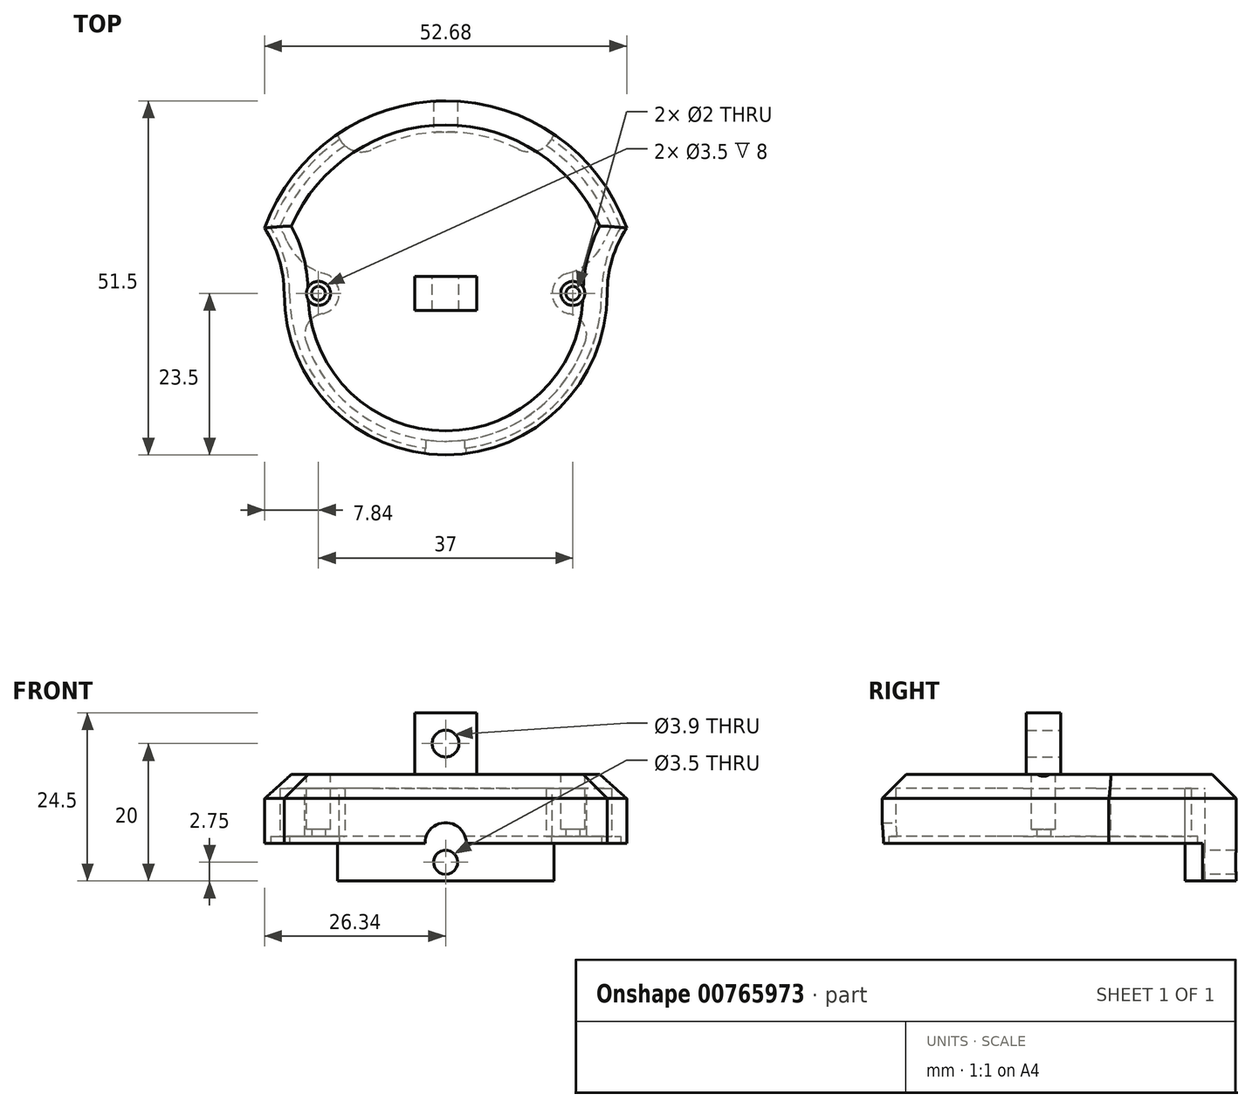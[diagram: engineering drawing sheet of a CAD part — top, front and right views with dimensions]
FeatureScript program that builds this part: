
annotation { "Feature Type Name" : "Feature", "Feature Type Description" : "" }
export const myFeature = defineFeature(function(context is Context, id is Id, definition is map)
    precondition{}
    {
        {
            var Q0;
            Q0=qCreatedBy(makeId("Top.planeOp"),FACE);
            var sketch = newSketch(context, id + "F0", { "sketchPlane" : qUnion([Q0])});
            skCircle(sketch, "E0", {"center": v(0, 0) * mm, "radius": 23.5 * mm, "construction": true});
            skCircle(sketch, "E1", {"center": v(0, 0) * mm, "radius": 28 * mm, "construction": true});
            skLineSegment(sketch, "E2", {"start": v(-26.34, 9.5) * mm, "end": v(26.34, 9.5) * mm, "construction": true});
            skArc(sketch, "E3", {"start": v(-23.5, 0) * mm, "mid": v(0, -23.5) * mm, "end": v(23.5, 0) * mm});
            skArc(sketch, "E4", {"start": v(-26.34, 9.5) * mm, "mid": v(0, 28) * mm, "end": v(26.34, 9.5) * mm});
            skArc(sketch, "E5", {"start": v(-23.5, 0) * mm, "mid": v(-24.22, 4.96) * mm, "end": v(-26.34, 9.5) * mm});
            skArc(sketch, "E6", {"start": v(26.34, 9.5) * mm, "mid": v(24.22, 4.96) * mm, "end": v(23.5, 0) * mm});
            skCircle(sketch, "E7", {"center": v(-18.5, 0) * mm, "radius": 1 * mm});
            skCircle(sketch, "E8", {"center": v(18.5, 0) * mm, "radius": 1 * mm});
            skSolve(sketch);
        }
        {
            var Q0;
            Q0 = qSketchRegion(id + "F0", true);
            extrude(context, id + "F1", {"entities" : qUnion([Q0]), "endBound" : BoundingType.SYMMETRIC, "depth" : 10 * mm, "offsetDistance" : 25 * mm});
        }
        {
            var Q0;
            Q0=makeQuery(id+"F1.opExtrude","CAP_FACE",FACE,{"disambiguationData":[OSD([sQuery(id+"F0.wireOp",EDGE,"E3"),sQuery(id+"F0.wireOp",EDGE,"E4"),sQuery(id+"F0.wireOp",EDGE,"E5"),sQuery(id+"F0.wireOp",EDGE,"E6"),sQuery(id+"F0.wireOp",EDGE,"E7"),sQuery(id+"F0.wireOp",EDGE,"E8")])],"isStart":true});
            var sketch = newSketch(context, id + "F2", { "sketchPlane" : qUnion([Q0])});
            skArc(sketch, "E9", {"start": v(-21.5, 0) * mm, "mid": v(0, 21.5) * mm, "end": v(21.5, 0) * mm});
            skArc(sketch, "E10", {"start": v(-24.12, -9.7) * mm, "mid": v(0, -26) * mm, "end": v(24.12, -9.7) * mm});
            skArc(sketch, "E11", {"start": v(21.5, 0) * mm, "mid": v(22.17, -5.02) * mm, "end": v(24.12, -9.7) * mm});
            skArc(sketch, "E12", {"start": v(-24.12, -9.7) * mm, "mid": v(-22.17, -5.02) * mm, "end": v(-21.5, 0) * mm});
            skSolve(sketch);
        }
        {
            var Q0;
            Q0 = qSketchRegion(id + "F2", true);
            extrude(context, id + "F3", {"entities" : qUnion([Q0]), "operationType" : NewBodyOperationType.REMOVE, "oppositeDirection" : true, "depth" : 8 * mm, "offsetDistance" : 25 * mm});
        }
        {
            var Q0;
            Q0=makeQuery(id+"F1.opExtrude","CAP_FACE",FACE,{"disambiguationData":[OSD([sQuery(id+"F0.wireOp",EDGE,"E3"),sQuery(id+"F0.wireOp",EDGE,"E4"),sQuery(id+"F0.wireOp",EDGE,"E5"),sQuery(id+"F0.wireOp",EDGE,"E6"),sQuery(id+"F0.wireOp",EDGE,"E7"),sQuery(id+"F0.wireOp",EDGE,"E8")])],"isStart":true});
            var sketch = newSketch(context, id + "F4", { "sketchPlane" : qUnion([Q0])});
            skArc(sketch, "E13", {"start": v(-22.7, 0) * mm, "mid": v(0, 22.7) * mm, "end": v(22.7, 0) * mm});
            skArc(sketch, "E14", {"start": v(-25.46, -9.58) * mm, "mid": v(0, -27.2) * mm, "end": v(25.46, -9.58) * mm});
            skArc(sketch, "E15", {"start": v(-25.46, -9.58) * mm, "mid": v(-23.4, -4.99) * mm, "end": v(-22.7, 0) * mm});
            skArc(sketch, "E16", {"start": v(22.7, 0) * mm, "mid": v(23.4, -4.99) * mm, "end": v(25.46, -9.58) * mm});
            skSolve(sketch);
        }
        {
            var Q0;
            Q0 = qSketchRegion(id + "F4", true);
            extrude(context, id + "F5", {"entities" : qUnion([Q0]), "operationType" : NewBodyOperationType.REMOVE, "oppositeDirection" : true, "depth" : 1 * mm, "offsetDistance" : 25 * mm});
        }
        {
            var Q0;
            Q0=makeQuery(id+"F3.boolean.opBoolean","COPY",FACE,{"derivedFrom":makeQuery(id+"F3.opExtrude","CAP_FACE",FACE,{"disambiguationData":[OSD([sQuery(id+"F2.wireOp",EDGE,"E9"),sQuery(id+"F2.wireOp",EDGE,"E10"),sQuery(id+"F2.wireOp",EDGE,"E11"),sQuery(id+"F2.wireOp",EDGE,"E12")])],"isStart":false})});
            var sketch = newSketch(context, id + "F6", { "sketchPlane" : qUnion([Q0])});
            skCircle(sketch, "E17", {"center": v(-18.5, 0) * mm, "radius": 1 * mm});
            skCircle(sketch, "E18", {"center": v(18.5, 0) * mm, "radius": 1 * mm});
            skArc(sketch, "E19", {"start": v(-17.97, 2.96) * mm, "mid": v(-15.5, 0.15) * mm, "end": v(-17.67, -2.89) * mm});
            skArc(sketch, "E20", {"start": v(17.97, 2.96) * mm, "mid": v(15.5, 0.15) * mm, "end": v(17.67, -2.89) * mm});
            skArc(sketch, "E21", {"start": v(-20.33, 6.99) * mm, "mid": v(-20.08, 4.43) * mm, "end": v(-17.97, 2.96) * mm});
            skArc(sketch, "E22", {"start": v(-17.67, -2.89) * mm, "mid": v(-20.91, -4.66) * mm, "end": v(-23.08, -7.64) * mm});
            skArc(sketch, "E23", {"start": v(23.08, -7.64) * mm, "mid": v(20.91, -4.66) * mm, "end": v(17.67, -2.89) * mm});
            skArc(sketch, "E24", {"start": v(17.97, 2.96) * mm, "mid": v(20.08, 4.43) * mm, "end": v(20.33, 6.99) * mm});
            skArc(sketch, "E25", {"start": v(-20.33, 6.99) * mm, "mid": v(-22.85, -0.11) * mm, "end": v(-23.08, -7.64) * mm});
            skArc(sketch, "E26", {"start": v(23.08, -7.64) * mm, "mid": v(22.92, -0.1) * mm, "end": v(20.33, 6.99) * mm});
            skSolve(sketch);
        }
        {
            var Q0;
            Q0 = qSketchRegion(id + "F6", true);
            var Q1;
            Q1=makeQuery(id+"F5.boolean.opBoolean","COPY",FACE,{"derivedFrom":makeQuery(id+"F5.opExtrude","CAP_FACE",FACE,{"disambiguationData":[OSD([sQuery(id+"F4.wireOp",EDGE,"E13"),sQuery(id+"F4.wireOp",EDGE,"E14"),sQuery(id+"F4.wireOp",EDGE,"E15"),sQuery(id+"F4.wireOp",EDGE,"E16")])],"isStart":false})});
            extrude(context, id + "F7", {"entities" : qUnion([Q0]), "operationType" : NewBodyOperationType.ADD, "endBound" : BoundingType.UP_TO_SURFACE, "depth" : 25 * mm, "endBoundEntityFace" : qUnion([Q1]), "offsetDistance" : 25 * mm});
        }
        {
            var Q0;
            Q0=makeQuery(id+"F1.opExtrude","CAP_FACE",FACE,{"disambiguationData":[OSD([sQuery(id+"F0.wireOp",EDGE,"E3"),sQuery(id+"F0.wireOp",EDGE,"E4"),sQuery(id+"F0.wireOp",EDGE,"E5"),sQuery(id+"F0.wireOp",EDGE,"E6"),sQuery(id+"F0.wireOp",EDGE,"E7"),sQuery(id+"F0.wireOp",EDGE,"E8")])],"isStart":false});
            var sketch = newSketch(context, id + "F8", { "sketchPlane" : qUnion([Q0])});
            skCircle(sketch, "E27", {"center": v(-18.5, 0) * mm, "radius": 1.75 * mm});
            skCircle(sketch, "E28", {"center": v(18.5, 0) * mm, "radius": 1.75 * mm});
            skSolve(sketch);
        }
        {
            var Q0;
            Q0 = qSketchRegion(id + "F8", true);
            extrude(context, id + "F9", {"entities" : qUnion([Q0]), "operationType" : NewBodyOperationType.REMOVE, "oppositeDirection" : true, "depth" : 8 * mm, "offsetDistance" : 25 * mm});
        }
        {
            var Q0;
            Q0=qCreatedBy(makeId("Front.planeOp"),FACE);
            var sketch = newSketch(context, id + "F10", { "sketchPlane" : qUnion([Q0])});
            skCircle(sketch, "E29", {"center": v(0, -5) * mm, "radius": 3 * mm});
            skSolve(sketch);
        }
        {
            var Q0;
            Q0 = qSketchRegion(id + "F10", true);
            extrude(context, id + "F11", {"entities" : qUnion([Q0]), "operationType" : NewBodyOperationType.REMOVE, "endBound" : BoundingType.THROUGH_ALL, "depth" : 25 * mm, "offsetDistance" : 25 * mm});
        }
        {
            var Q0;
            Q0=qCreatedBy(makeId("Front.planeOp"),FACE);
            var sketch = newSketch(context, id + "F12", { "sketchPlane" : qUnion([Q0])});
            skLineSegment(sketch, "E30.bottom", {"start": v(-4.5, 5) * mm, "end": v(4.5, 5) * mm});
            skLineSegment(sketch, "E30.top", {"start": v(-4.5, 14) * mm, "end": v(4.5, 14) * mm});
            skLineSegment(sketch, "E30.left", {"start": v(-4.5, 5) * mm, "end": v(-4.5, 14) * mm});
            skLineSegment(sketch, "E30.right", {"start": v(4.5, 5) * mm, "end": v(4.5, 14) * mm});
            skPoint(sketch, "E30.middle", {"position": v(0, 9.5) * mm});
            skCircle(sketch, "E31", {"center": v(0, 9.5) * mm, "radius": 1.95 * mm});
            skSolve(sketch);
        }
        {
            var Q0;
            Q0 = qSketchRegion(id + "F12", true);
            extrude(context, id + "F13", {"entities" : qUnion([Q0]), "operationType" : NewBodyOperationType.ADD, "endBound" : BoundingType.SYMMETRIC, "depth" : 5 * mm, "offsetDistance" : 25 * mm});
        }
        {
            var Q0;
            Q0=qCreatedBy(makeId("Front.planeOp"),FACE);
            var sketch = newSketch(context, id + "F14", { "sketchPlane" : qUnion([Q0])});
            skCircle(sketch, "E32.cCircle", {"center": v(0, 9.5) * mm, "radius": 3.45 * mm, "construction": true});
            skLineSegment(sketch, "E32.0", {"start": v(3.45, 7.5) * mm, "end": v(0, 5.52) * mm});
            skLineSegment(sketch, "E32.1", {"start": v(0, 5.52) * mm, "end": v(-3.45, 7.5) * mm});
            skLineSegment(sketch, "E32.2", {"start": v(-3.45, 7.5) * mm, "end": v(-3.45, 11.5) * mm});
            skLineSegment(sketch, "E32.3", {"start": v(-3.45, 11.5) * mm, "end": v(0, 13.48) * mm});
            skLineSegment(sketch, "E32.4", {"start": v(0, 13.48) * mm, "end": v(3.45, 11.5) * mm});
            skLineSegment(sketch, "E32.5", {"start": v(3.45, 11.5) * mm, "end": v(3.45, 7.5) * mm});
            skPoint(sketch, "E32.0.midPoint", {"position": v(1.73, 6.51) * mm});
            skLineSegment(sketch, "E33", {"start": v(3.45, 11.5) * mm, "end": v(3.45, 14) * mm});
            skLineSegment(sketch, "E34", {"start": v(3.45, 14) * mm, "end": v(-3.45, 14) * mm});
            skLineSegment(sketch, "E35", {"start": v(-3.45, 14) * mm, "end": v(-3.45, 11.5) * mm});
            skSolve(sketch);
        }
        {
            var Q0;
            Q0=makeQuery(id+"F7.boolean.opBoolean","MERGE",FACE,{"derivedFrom":[makeQuery(id+"F5.boolean.opBoolean","COPY",FACE,{"derivedFrom":makeQuery(id+"F5.opExtrude","CAP_FACE",FACE,{"disambiguationData":[OSD([sQuery(id+"F4.wireOp",EDGE,"E13"),sQuery(id+"F4.wireOp",EDGE,"E14"),sQuery(id+"F4.wireOp",EDGE,"E15"),sQuery(id+"F4.wireOp",EDGE,"E16")])],"isStart":false})}),makeQuery(id+"F7.opExtrude","CAP_FACE",FACE,{"disambiguationData":[OSD([sQuery(id+"F6.wireOp",EDGE,"E17"),sQuery(id+"F6.wireOp",EDGE,"E19"),sQuery(id+"F6.wireOp",EDGE,"E21"),sQuery(id+"F6.wireOp",EDGE,"E22"),sQuery(id+"F6.wireOp",EDGE,"E25")])],"isStart":false}),makeQuery(id+"F7.opExtrude","CAP_FACE",FACE,{"disambiguationData":[OSD([sQuery(id+"F6.wireOp",EDGE,"E18"),sQuery(id+"F6.wireOp",EDGE,"E20"),sQuery(id+"F6.wireOp",EDGE,"E23"),sQuery(id+"F6.wireOp",EDGE,"E24"),sQuery(id+"F6.wireOp",EDGE,"E26")])],"isStart":false})]});
            var sketch = newSketch(context, id + "F15", { "sketchPlane" : qUnion([Q0])});
            skLineSegment(sketch, "E36", {"start": v(-15.75, -23.15) * mm, "end": v(15.75, -23.15) * mm, "construction": true});
            skCircle(sketch, "E37", {"center": v(0, 0) * mm, "radius": 23.5 * mm, "construction": true});
            skArc(sketch, "E38", {"start": v(-10.57, -20.99) * mm, "mid": v(-13.66, -20.88) * mm, "end": v(-15.75, -23.15) * mm});
            skArc(sketch, "E39", {"start": v(15.75, -23.15) * mm, "mid": v(13.66, -20.88) * mm, "end": v(10.57, -20.99) * mm});
            skArc(sketch, "E40", {"start": v(-10.57, -20.99) * mm, "mid": v(0, -23.5) * mm, "end": v(10.57, -20.99) * mm});
            skArc(sketch, "E41", {"start": v(-15.75, -23.15) * mm, "mid": v(0, -28) * mm, "end": v(15.75, -23.15) * mm});
            skSolve(sketch);
        }
        {
            var Q0;
            Q0 = qSketchRegion(id + "F15", true);
            extrude(context, id + "F16", {"entities" : qUnion([Q0]), "operationType" : NewBodyOperationType.ADD, "depth" : 6.5 * mm, "offsetDistance" : 25 * mm});
        }
        {
            var Q0;
            Q0 = qSketchRegion(id + "F15", true);
            var Q1;
            Q1=makeQuery(id+"F3.boolean.opBoolean","COPY",FACE,{"derivedFrom":makeQuery(id+"F3.opExtrude","CAP_FACE",FACE,{"disambiguationData":[OSD([sQuery(id+"F2.wireOp",EDGE,"E9"),sQuery(id+"F2.wireOp",EDGE,"E10"),sQuery(id+"F2.wireOp",EDGE,"E11"),sQuery(id+"F2.wireOp",EDGE,"E12")])],"isStart":false})});
            extrude(context, id + "F17", {"entities" : qUnion([Q0]), "operationType" : NewBodyOperationType.ADD, "endBound" : BoundingType.UP_TO_SURFACE, "oppositeDirection" : true, "depth" : 25 * mm, "endBoundEntityFace" : qUnion([Q1]), "offsetDistance" : 25 * mm});
        }
        {
            var Q0;
            Q0=qCreatedBy(makeId("Front.planeOp"),FACE);
            var sketch = newSketch(context, id + "F18", { "sketchPlane" : qUnion([Q0])});
            skCircle(sketch, "E42", {"center": v(0, -7.75) * mm, "radius": 1.75 * mm});
            skLineSegment(sketch, "E43", {"start": v(0, -10.5) * mm, "end": v(0, -7.75) * mm, "construction": true});
            skLineSegment(sketch, "E44", {"start": v(0, -5) * mm, "end": v(0, -7.75) * mm, "construction": true});
            skSolve(sketch);
        }
        {
            var Q0;
            Q0 = qSketchRegion(id + "F18", true);
            extrude(context, id + "F19", {"entities" : qUnion([Q0]), "operationType" : NewBodyOperationType.REMOVE, "endBound" : BoundingType.THROUGH_ALL, "oppositeDirection" : true, "depth" : 25 * mm, "offsetDistance" : 25 * mm});
        }
        {
            var Q0;
            Q0=makeQuery(id+"F1.opExtrude","CAP_EDGE",EDGE,{"disambiguationData":[OSD([sQuery(id+"F0.wireOp",EDGE,"E3")])],"isStart":false});
            var Q1;
            Q1=makeQuery(id+"F1.opExtrude","CAP_EDGE",EDGE,{"disambiguationData":[OSD([sQuery(id+"F0.wireOp",EDGE,"E6")])],"isStart":false});
            var Q2;
            Q2=makeQuery(id+"F1.opExtrude","CAP_EDGE",EDGE,{"disambiguationData":[OSD([sQuery(id+"F0.wireOp",EDGE,"E4")])],"isStart":false});
            var Q3;
            Q3=makeQuery(id+"F1.opExtrude","CAP_EDGE",EDGE,{"disambiguationData":[OSD([sQuery(id+"F0.wireOp",EDGE,"E5")])],"isStart":false});
            chamfer(context, id + "F20", {"entities" : qUnion([Q0, Q1, Q2, Q3]), "width" : 3.5 * mm, "tangentPropagation" : true});
        }
    });
